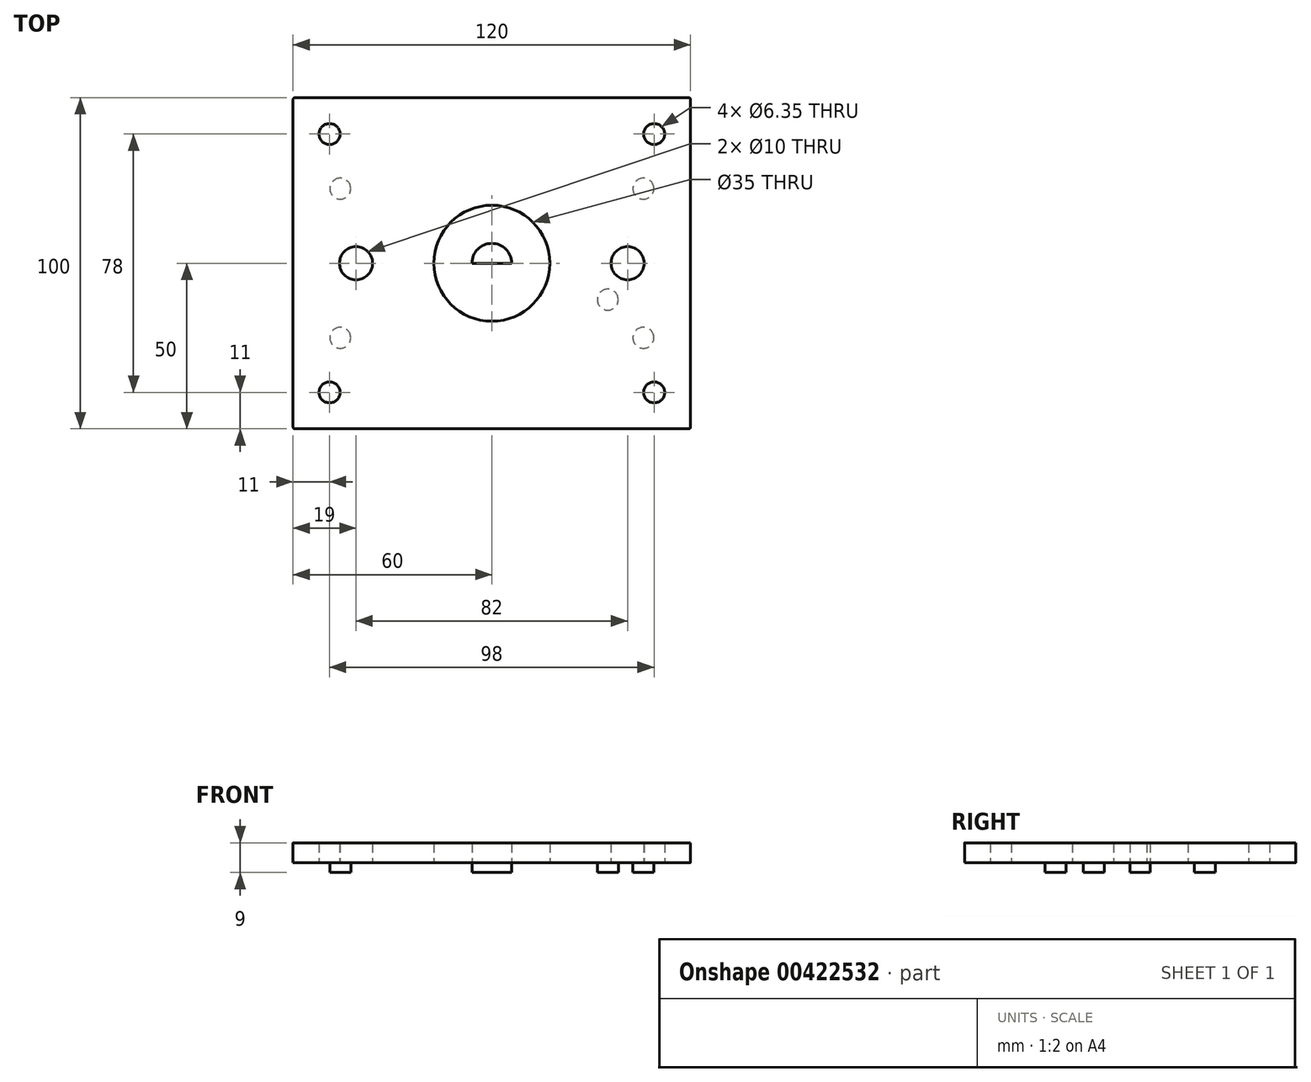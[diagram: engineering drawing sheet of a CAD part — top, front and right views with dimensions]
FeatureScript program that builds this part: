
annotation { "Feature Type Name" : "Feature", "Feature Type Description" : "" }
export const myFeature = defineFeature(function(context is Context, id is Id, definition is map)
    precondition{}
    {
        {
            var Q0;
            Q0=qCreatedBy(makeId("Top.planeOp"),FACE);
            var sketch = newSketch(context, id + "F0", { "sketchPlane" : qUnion([Q0])});
            skLineSegment(sketch, "E0", {"start": v(0, 60) * mm, "end": v(0, -60) * mm});
            skLineSegment(sketch, "E1", {"start": v(-70, 0) * mm, "end": v(70, 0) * mm});
            skLineSegment(sketch, "E2", {"start": v(-60, 50) * mm, "end": v(-60, -50) * mm});
            skLineSegment(sketch, "E3", {"start": v(60, 50) * mm, "end": v(60, -50) * mm});
            skLineSegment(sketch, "E4", {"start": v(-60, 50) * mm, "end": v(60, 50) * mm});
            skLineSegment(sketch, "E5", {"start": v(-60, -50) * mm, "end": v(60, -50) * mm});
            skCircle(sketch, "E6", {"center": v(0, 0) * mm, "radius": 6 * mm});
            skCircle(sketch, "E7", {"center": v(-45.77, 22.5) * mm, "radius": 3.17 * mm});
            skCircle(sketch, "E8", {"center": v(-45.77, -22.5) * mm, "radius": 3.17 * mm});
            skCircle(sketch, "E9", {"center": v(45.77, -22.5) * mm, "radius": 3.17 * mm});
            skCircle(sketch, "E10", {"center": v(45.77, 22.5) * mm, "radius": 3.17 * mm});
            skCircle(sketch, "E11", {"center": v(-41, 0) * mm, "radius": 2.58 * mm});
            skCircle(sketch, "E12", {"center": v(41, 0) * mm, "radius": 2.58 * mm});
            skCircle(sketch, "E13", {"center": v(-41, 0) * mm, "radius": 5 * mm});
            skCircle(sketch, "E14", {"center": v(41, 0) * mm, "radius": 5 * mm});
            skCircle(sketch, "E15", {"center": v(-49, -39) * mm, "radius": 3.17 * mm});
            skCircle(sketch, "E16", {"center": v(49, -39) * mm, "radius": 3.17 * mm});
            skCircle(sketch, "E17", {"center": v(-49, 39) * mm, "radius": 3.17 * mm});
            skCircle(sketch, "E18", {"center": v(49, 39) * mm, "radius": 3.17 * mm});
            skCircle(sketch, "E19", {"center": v(0, 0) * mm, "radius": 17.5 * mm});
            skCircle(sketch, "E20", {"center": v(35, -11) * mm, "radius": 8 * mm});
            skCircle(sketch, "E21", {"center": v(35, -11) * mm, "radius": 3.17 * mm});
            skSolve(sketch);
        }
        {
            var Q0;
            Q0=makeQuery(id+"F0.imprint","IMPRINT",FACE,{"disambiguationData":[TD([[makeQuery(id+"F0.imprint","IMPRINT",EDGE,{"derivedFrom":sQuery(id+"F0.wireOp",EDGE,"E7")}),1.0]])]});
            var Q1;
            Q1=makeQuery(id+"F0.imprint","IMPRINT",FACE,{"disambiguationData":[TD([[makeQuery(id+"F0.imprint","IMPRINT",EDGE,{"derivedFrom":sQuery(id+"F0.wireOp",EDGE,"E10")}),1.0]])]});
            var Q2;
            Q2=makeQuery(id+"F0.imprint","IMPRINT",FACE,{"disambiguationData":[TD([[makeQuery(id+"F0.imprint","IMPRINT",EDGE,{"derivedFrom":sQuery(id+"F0.wireOp",EDGE,"E9")}),1.0]])]});
            var Q3;
            Q3=makeQuery(id+"F0.imprint","IMPRINT",FACE,{"disambiguationData":[TD([[makeQuery(id+"F0.imprint","IMPRINT",EDGE,{"derivedFrom":sQuery(id+"F0.wireOp",EDGE,"E8")}),1.0]])]});
            var Q4;
            Q4=makeQuery(id+"F0.imprint","IMPRINT",FACE,{"disambiguationData":[TD([[makeQuery(id+"F0.imprint","IMPRINT",EDGE,{"derivedFrom":sQuery(id+"F0.wireOp",EDGE,"E21")}),1.0]])]});
            var Q5;
            {var subQ0=sQuery(id+"F0.wireOp",EDGE,"E14");var subQ1=sQuery(id+"F0.wireOp",EDGE,"E1");var subQ8=makeQuery(id+"F0.imprint","INTERSECT",VERTEX,{"disambiguationData":[OD(0.0)],"derivedFrom":[subQ1,subQ0]});Q5=makeQuery(id+"F0.imprint","IMPRINT",FACE,{"disambiguationData":[TD([[makeQuery(id+"F0.imprint","IMPRINT",EDGE,{"disambiguationData":[TD([[subQ8,-1.0]])],"derivedFrom":subQ1}),-1.0]])]});}
            var Q6;
            {var subQ0=sQuery(id+"F0.wireOp",EDGE,"E14");var subQ1=sQuery(id+"F0.wireOp",EDGE,"E1");var subQ2=makeQuery(id+"F0.imprint","INTERSECT",VERTEX,{"disambiguationData":[OD(0.0)],"derivedFrom":[subQ1,subQ0]});Q6=makeQuery(id+"F0.imprint","IMPRINT",FACE,{"disambiguationData":[TD([[makeQuery(id+"F0.imprint","IMPRINT",EDGE,{"disambiguationData":[TD([[subQ2,-1.0]])],"derivedFrom":subQ1}),1.0]])]});}
            var Q7;
            {var subQ0=sQuery(id+"F0.wireOp",EDGE,"E13");var subQ1=sQuery(id+"F0.wireOp",EDGE,"E1");var subQ2=makeQuery(id+"F0.imprint","INTERSECT",VERTEX,{"disambiguationData":[OD(0.0)],"derivedFrom":[subQ1,subQ0]});Q7=makeQuery(id+"F0.imprint","IMPRINT",FACE,{"disambiguationData":[TD([[makeQuery(id+"F0.imprint","IMPRINT",EDGE,{"disambiguationData":[TD([[subQ2,-1.0]])],"derivedFrom":subQ1}),1.0]])]});}
            var Q8;
            {var subQ0=sQuery(id+"F0.wireOp",EDGE,"E13");var subQ1=sQuery(id+"F0.wireOp",EDGE,"E1");var subQ2=makeQuery(id+"F0.imprint","INTERSECT",VERTEX,{"disambiguationData":[OD(0.0)],"derivedFrom":[subQ1,subQ0]});Q8=makeQuery(id+"F0.imprint","IMPRINT",FACE,{"disambiguationData":[TD([[makeQuery(id+"F0.imprint","IMPRINT",EDGE,{"disambiguationData":[TD([[subQ2,-1.0]])],"derivedFrom":subQ1}),-1.0]])]});}
            var Q9;
            {var subQ0=sQuery(id+"F0.wireOp",EDGE,"E20");var subQ1=sQuery(id+"F0.wireOp",EDGE,"E14");var subQ2=makeQuery(id+"F0.imprint","INTERSECT",VERTEX,{"disambiguationData":[OD(0.0)],"derivedFrom":[subQ1,subQ0]});Q9=makeQuery(id+"F0.imprint","IMPRINT",FACE,{"disambiguationData":[TD([[makeQuery(id+"F0.imprint","IMPRINT",EDGE,{"disambiguationData":[TD([[subQ2,-1.0]])],"derivedFrom":subQ1}),-1.0]])]});}
            var Q10;
            {var subQ0=sQuery(id+"F0.wireOp",EDGE,"E19");var subQ1=sQuery(id+"F0.wireOp",EDGE,"E0");var subQ2=makeQuery(id+"F0.imprint","INTERSECT",VERTEX,{"disambiguationData":[OD(0.0)],"derivedFrom":[subQ1,subQ0]});Q10=makeQuery(id+"F0.imprint","IMPRINT",FACE,{"disambiguationData":[TD([[makeQuery(id+"F0.imprint","IMPRINT",EDGE,{"disambiguationData":[TD([[subQ2,-1.0]])],"derivedFrom":subQ1}),-1.0]])]});}
            var Q11;
            {var subQ0=sQuery(id+"F0.wireOp",EDGE,"E19");var subQ1=sQuery(id+"F0.wireOp",EDGE,"E0");var subQ2=makeQuery(id+"F0.imprint","INTERSECT",VERTEX,{"disambiguationData":[OD(0.0)],"derivedFrom":[subQ1,subQ0]});Q11=makeQuery(id+"F0.imprint","IMPRINT",FACE,{"disambiguationData":[TD([[makeQuery(id+"F0.imprint","IMPRINT",EDGE,{"disambiguationData":[TD([[subQ2,-1.0]])],"derivedFrom":subQ1}),1.0]])]});}
            var Q12;
            {var subQ0=sQuery(id+"F0.wireOp",EDGE,"E6");var subQ1=sQuery(id+"F0.wireOp",EDGE,"E0");var subQ2=makeQuery(id+"F0.imprint","INTERSECT",VERTEX,{"disambiguationData":[OD(1.0)],"derivedFrom":[subQ1,subQ0]});Q12=makeQuery(id+"F0.imprint","IMPRINT",FACE,{"disambiguationData":[TD([[makeQuery(id+"F0.imprint","IMPRINT",EDGE,{"disambiguationData":[TD([[subQ2,-1.0]])],"derivedFrom":subQ1}),1.0]])]});}
            var Q13;
            {var subQ0=sQuery(id+"F0.wireOp",EDGE,"E6");var subQ1=sQuery(id+"F0.wireOp",EDGE,"E0");var subQ2=makeQuery(id+"F0.imprint","INTERSECT",VERTEX,{"disambiguationData":[OD(1.0)],"derivedFrom":[subQ1,subQ0]});Q13=makeQuery(id+"F0.imprint","IMPRINT",FACE,{"disambiguationData":[TD([[makeQuery(id+"F0.imprint","IMPRINT",EDGE,{"disambiguationData":[TD([[subQ2,-1.0]])],"derivedFrom":subQ1}),-1.0]])]});}
            extrude(context, id + "F1", {"entities" : qUnion([Q0, Q1, Q2, Q3, Q4, Q5, Q6, Q7, Q8, Q9, Q10, Q11, Q12, Q13]), "depth" : 9 * mm});
        }
        {
            var Q0;
            {var subQ0=sQuery(id+"F0.wireOp",EDGE,"E14");var subQ1=sQuery(id+"F0.wireOp",EDGE,"E1");var subQ8=makeQuery(id+"F0.imprint","INTERSECT",VERTEX,{"disambiguationData":[OD(0.0)],"derivedFrom":[subQ1,subQ0]});Q0=makeQuery(id+"F0.imprint","IMPRINT",FACE,{"disambiguationData":[TD([[makeQuery(id+"F0.imprint","IMPRINT",EDGE,{"disambiguationData":[TD([[subQ8,-1.0]])],"derivedFrom":subQ1}),-1.0]])]});}
            var Q1;
            {var subQ0=sQuery(id+"F0.wireOp",EDGE,"E14");var subQ1=sQuery(id+"F0.wireOp",EDGE,"E1");var subQ2=makeQuery(id+"F0.imprint","INTERSECT",VERTEX,{"disambiguationData":[OD(0.0)],"derivedFrom":[subQ1,subQ0]});Q1=makeQuery(id+"F0.imprint","IMPRINT",FACE,{"disambiguationData":[TD([[makeQuery(id+"F0.imprint","IMPRINT",EDGE,{"disambiguationData":[TD([[subQ2,-1.0]])],"derivedFrom":subQ1}),1.0]])]});}
            var Q2;
            {var subQ0=sQuery(id+"F0.wireOp",EDGE,"E20");var subQ1=sQuery(id+"F0.wireOp",EDGE,"E14");var subQ2=makeQuery(id+"F0.imprint","INTERSECT",VERTEX,{"disambiguationData":[OD(0.0)],"derivedFrom":[subQ1,subQ0]});Q2=makeQuery(id+"F0.imprint","IMPRINT",FACE,{"disambiguationData":[TD([[makeQuery(id+"F0.imprint","IMPRINT",EDGE,{"disambiguationData":[TD([[subQ2,-1.0]])],"derivedFrom":subQ1}),-1.0]])]});}
            var Q3;
            {var subQ0=sQuery(id+"F0.wireOp",EDGE,"E13");var subQ1=sQuery(id+"F0.wireOp",EDGE,"E1");var subQ2=makeQuery(id+"F0.imprint","INTERSECT",VERTEX,{"disambiguationData":[OD(0.0)],"derivedFrom":[subQ1,subQ0]});Q3=makeQuery(id+"F0.imprint","IMPRINT",FACE,{"disambiguationData":[TD([[makeQuery(id+"F0.imprint","IMPRINT",EDGE,{"disambiguationData":[TD([[subQ2,-1.0]])],"derivedFrom":subQ1}),1.0]])]});}
            var Q4;
            {var subQ0=sQuery(id+"F0.wireOp",EDGE,"E13");var subQ1=sQuery(id+"F0.wireOp",EDGE,"E1");var subQ2=makeQuery(id+"F0.imprint","INTERSECT",VERTEX,{"disambiguationData":[OD(0.0)],"derivedFrom":[subQ1,subQ0]});Q4=makeQuery(id+"F0.imprint","IMPRINT",FACE,{"disambiguationData":[TD([[makeQuery(id+"F0.imprint","IMPRINT",EDGE,{"disambiguationData":[TD([[subQ2,-1.0]])],"derivedFrom":subQ1}),-1.0]])]});}
            extrude(context, id + "F2", {"entities" : qUnion([Q0, Q1, Q2, Q3, Q4]), "depth" : 3 * mm});
        }
        {
            var Q0;
            Q0=makeQuery(id+"F2.opExtrude","SWEPT_BODY",BODY,{"disambiguationData":[OSD([sQuery(id+"F0.wireOp",EDGE,"E11"),sQuery(id+"F0.wireOp",EDGE,"E13")])]});
            var Q1;
            Q1=makeQuery(id+"F2.opExtrude","SWEPT_BODY",BODY,{"disambiguationData":[OSD([sQuery(id+"F0.wireOp",EDGE,"E12"),sQuery(id+"F0.wireOp",EDGE,"E14")])]});
            var Q2;
            Q2=makeQuery(id+"F1.opExtrude","SWEPT_BODY",BODY,{"disambiguationData":[OSD([sQuery(id+"F0.wireOp",EDGE,"E2"),sQuery(id+"F0.wireOp",EDGE,"E3"),sQuery(id+"F0.wireOp",EDGE,"E4"),sQuery(id+"F0.wireOp",EDGE,"E5"),sQuery(id+"F0.wireOp",EDGE,"E6"),sQuery(id+"F0.wireOp",EDGE,"E7"),sQuery(id+"F0.wireOp",EDGE,"E8"),sQuery(id+"F0.wireOp",EDGE,"E9"),sQuery(id+"F0.wireOp",EDGE,"E10"),sQuery(id+"F0.wireOp",EDGE,"E11"),sQuery(id+"F0.wireOp",EDGE,"E12"),sQuery(id+"F0.wireOp",EDGE,"E15"),sQuery(id+"F0.wireOp",EDGE,"E16"),sQuery(id+"F0.wireOp",EDGE,"E17"),sQuery(id+"F0.wireOp",EDGE,"E18"),sQuery(id+"F0.wireOp",EDGE,"E21")])]});
            booleanBodies(context, id + "F3", {"operationType" : BooleanOperationType.SUBTRACTION, "tools" : qUnion([Q0, Q1]), "targets" : qUnion([Q2])});
        }
        {
            var Q0;
            Q0=makeQuery(id+"F1.opExtrude","SWEPT_EDGE",EDGE,{"disambiguationData":[OSD([sQuery(id+"F0.wireOp",EDGE,"E3"),sQuery(id+"F0.wireOp",EDGE,"E4")])]});
            var Q1;
            Q1=makeQuery(id+"F1.opExtrude","SWEPT_EDGE",EDGE,{"disambiguationData":[OSD([sQuery(id+"F0.wireOp",EDGE,"E3"),sQuery(id+"F0.wireOp",EDGE,"E5")])]});
            var Q2;
            Q2=makeQuery(id+"F1.opExtrude","SWEPT_EDGE",EDGE,{"disambiguationData":[OSD([sQuery(id+"F0.wireOp",EDGE,"E2"),sQuery(id+"F0.wireOp",EDGE,"E4")])]});
            var Q3;
            Q3=makeQuery(id+"F1.opExtrude","SWEPT_EDGE",EDGE,{"disambiguationData":[OSD([sQuery(id+"F0.wireOp",EDGE,"E2"),sQuery(id+"F0.wireOp",EDGE,"E5")])]});
            fillet(context, id + "F4", {"entities" : qUnion([Q0, Q1, Q2, Q3]), "radius" : .5 * mm, "tangentPropagation" : true, "allowEdgeOverflow" : false});
        }
    });
